# Revit family: BE_70729_de_DE
name_source: partatom
category: Leuchten
units: mm (PartAtom-declared; Revit-internal decimal feet)

## family parameters
Basisbauteil = Fläche
Beim Laden mit Abzugskörper schneiden = Ja
Bemaßung runder Anschluss = Durchmesser verwenden
Gemeinsam genutzt = Nein
Lichtquelle = Nein
Raumberechnungspunkt = Ja
Teiletyp = Normal

## types (1)
- BEGA_70729_Grafit
    Aktualisierung = 2022-05-19T04:00:07
    BEGA_Dummy = Nein
    Beschreibung = Lichtmast
    Beschreibung_Sonderanfertigung = Hier können Sie Informationen zur Sonderanfertigung eintragen.
    Bestellnummer = 70729
    Gewicht = 21.4 kg
    Hersteller = BEGA
    Lastklassifizierung = Beleuchtung
    Logo = BEGA_Logo.png
    Material_01 = BEGA_Oberfläche_Grafit_matt
    Material_05 = BEGA_Oberfläche_Aluminium Guss
    Material_06 = BEGA_Oberfläche_Edelstahl_gebürstet
    Modell = 70729
    Produktdatenblatt = https://cdn.bega.com
    Scheinlast = 0 VA
    Sonderanfertigung = Nein
    Typenbild = 70729.png
    URL = https://www.bega.com
    Vorgabe-Ansicht = 0 mm  [stored 0 ft]

note: [stored X ft] marks values corroborated as IEEE doubles in the binary element streams (Revit-internal decimal feet)
